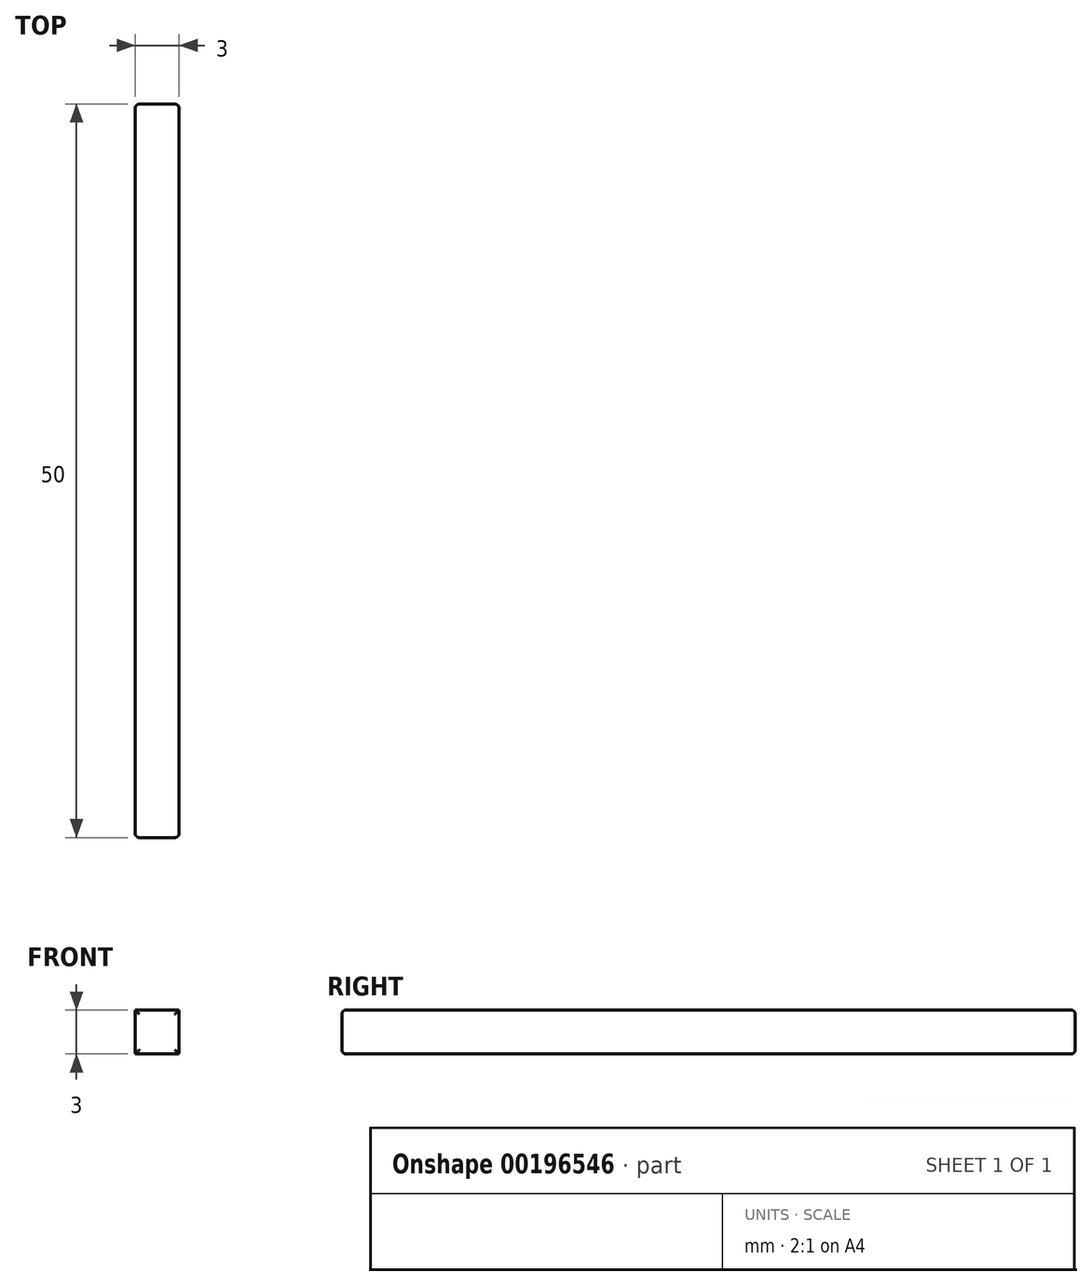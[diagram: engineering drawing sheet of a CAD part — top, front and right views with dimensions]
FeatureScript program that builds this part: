
annotation { "Feature Type Name" : "Feature", "Feature Type Description" : "" }
export const myFeature = defineFeature(function(context is Context, id is Id, definition is map)
    precondition{}
    {
        {
            var Q0;
            Q0=qCreatedBy(makeId("Front.planeOp"),FACE);
            var sketch = newSketch(context, id + "F0", { "sketchPlane" : qUnion([Q0])});
            skLineSegment(sketch, "E0.bottom", {"start": v(-1.5, 3) * mm, "end": v(1.5, 3) * mm});
            skLineSegment(sketch, "E0.top", {"start": v(-1.5, 0) * mm, "end": v(1.5, 0) * mm});
            skLineSegment(sketch, "E0.left", {"start": v(-1.5, 3) * mm, "end": v(-1.5, 0) * mm});
            skLineSegment(sketch, "E0.right", {"start": v(1.5, 3) * mm, "end": v(1.5, 0) * mm});
            skSolve(sketch);
        }
        {
            var Q0;
            Q0=qSketchRegion(id+"F0",true);
            extrude(context, id + "F1", {"entities" : qUnion([Q0]), "depth" : 50 * mm});
        }
        {
            var Q0;
            Q0=makeQuery(id+"F1.opExtrude","CAP_EDGE",EDGE,{"disambiguationData":[OSD([sQuery(id+"F0.wireOp",EDGE,"E0.bottom")])],"isStart":true});
            var Q1;
            Q1=makeQuery(id+"F1.opExtrude","CAP_EDGE",EDGE,{"disambiguationData":[OSD([sQuery(id+"F0.wireOp",EDGE,"E0.left")])],"isStart":true});
            var Q2;
            Q2=makeQuery(id+"F1.opExtrude","CAP_EDGE",EDGE,{"disambiguationData":[OSD([sQuery(id+"F0.wireOp",EDGE,"E0.right")])],"isStart":true});
            var Q3;
            Q3=makeQuery(id+"F1.opExtrude","CAP_EDGE",EDGE,{"disambiguationData":[OSD([sQuery(id+"F0.wireOp",EDGE,"E0.top")])],"isStart":true});
            var Q4;
            Q4=makeQuery(id+"F1.opExtrude","CAP_EDGE",EDGE,{"disambiguationData":[OSD([sQuery(id+"F0.wireOp",EDGE,"E0.bottom")])],"isStart":false});
            var Q5;
            Q5=makeQuery(id+"F1.opExtrude","CAP_EDGE",EDGE,{"disambiguationData":[OSD([sQuery(id+"F0.wireOp",EDGE,"E0.right")])],"isStart":false});
            var Q6;
            Q6=makeQuery(id+"F1.opExtrude","CAP_EDGE",EDGE,{"disambiguationData":[OSD([sQuery(id+"F0.wireOp",EDGE,"E0.left")])],"isStart":false});
            var Q7;
            Q7=makeQuery(id+"F1.opExtrude","CAP_FACE",FACE,{"disambiguationData":[OSD([sQuery(id+"F0.wireOp",EDGE,"E0.bottom"),sQuery(id+"F0.wireOp",EDGE,"E0.top"),sQuery(id+"F0.wireOp",EDGE,"E0.left"),sQuery(id+"F0.wireOp",EDGE,"E0.right")])],"isStart":false});
            fillet(context, id + "F2", {"entities" : qUnion([Q0, Q1, Q2, Q3, Q4, Q5, Q6, Q7]), "radius" : 0.3 * mm, "tangentPropagation" : true, "allowEdgeOverflow" : false});
        }
    });
